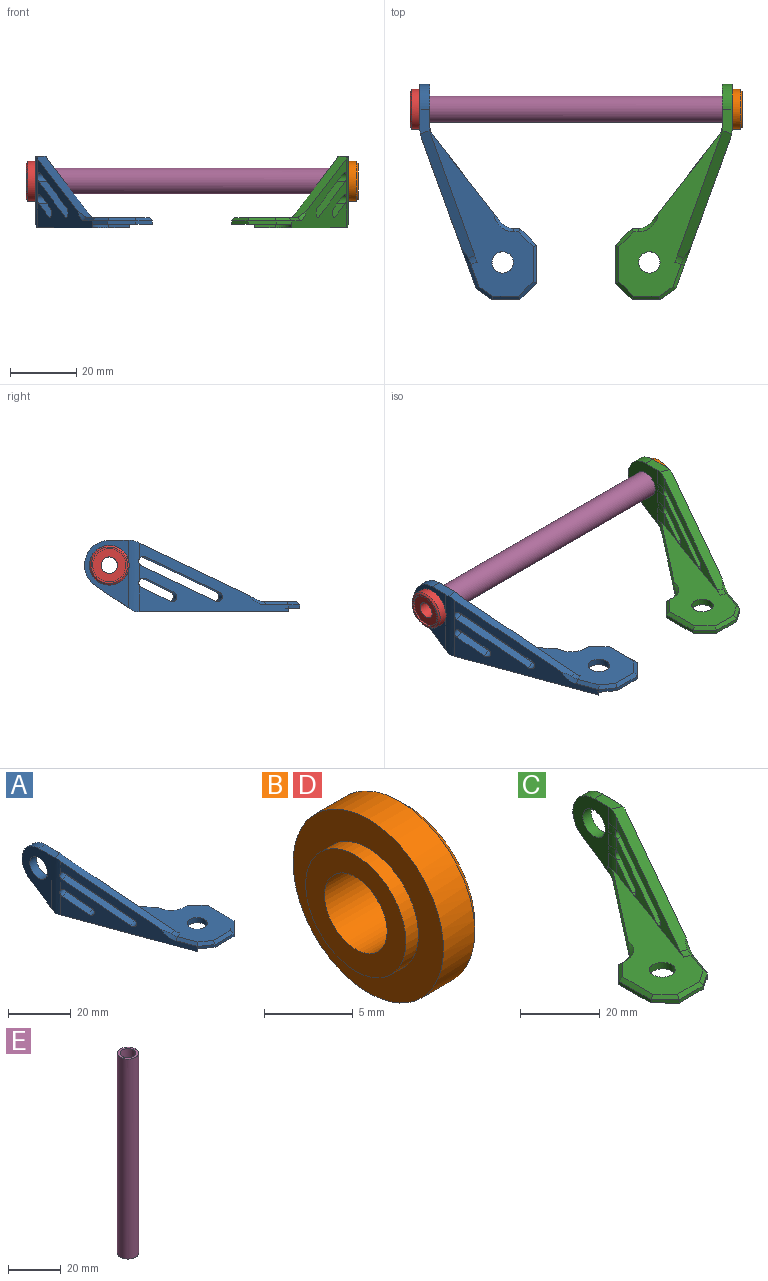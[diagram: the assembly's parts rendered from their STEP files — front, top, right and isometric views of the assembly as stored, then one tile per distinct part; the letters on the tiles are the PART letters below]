
ASSEMBLY  parts=5 mates=3
PART A: 51 faces, bbox 35.9x65.7x22.2 mm
  f0: plane 11.45x1mm, normal (1,0,0), area 11.4mm2, adj f35,f36,f40,f46
  f1: cylinder r=3.23mm len=6.45mm, axis (0,0,-1), area 40.5mm2, adj f2,f40
  f2: plane 51.56x31.22mm, normal (0,0,1), area 480.9mm2, adj f1,f6,f7,f8,f12,f24,f26,f33
  f3: plane 8.52x1mm, normal (0,-1,0), area 8.5mm2, adj f34,f36,f40,f44
  f4: plane 46.71x28.19mm, normal (0,0,-1), area 339.8mm2, adj f5,f9,f25,f32,f33,f37,f38,f39
  f5: plane 11.72x7.82mm, normal (0,0.55,-0.83), area 42.6mm2, adj f4,f8,f11,f13,f25,f50
  f6: plane 37.58x17.47mm, normal (0.94,0.34,0), area 123.7mm2, adj f2,f15,f17,f18,f19,f24,f30
  f7: plane 23.11x10.9mm, normal (0.94,0.34,0), area 75.5mm2, adj f2,f16,f17,f19,f21,f22,f23,f28
  f8: plane 19.79x12.83mm, normal (1,0,0), area 135.2mm2, adj f2,f5,f10,f13,f14,f26,f27,f28
  f9: plane 45.05x20.71mm, normal (-0.94,-0.34,0), area 358.8mm2, adj f4,f15,f16,f17,f18,f19,f20,f21
  f10: plane 7.45x3.07mm, normal (0,0,1), area 20.8mm2, adj f8,f11,f13,f15,f25,f30
  f11: plane 20.33x13.24mm, normal (-1,0,0), area 146mm2, adj f5,f10,f13,f14,f25
  f12: plane 9.34x4.32mm, normal (0.94,0.34,0), area 20.8mm2, adj f2,f20,f21,f23,f26
  f13: cylinder r=7.5mm len=13.74mm, axis (-1,0,0), area 57.5mm2, adj f5,f8,f10,f11
  f14: cylinder r=4mm len=8mm, axis (-1,0,0), area 75.4mm2, adj f8,f11
  f15: plane 39.31x18.79mm, normal (0.14,-0.38,0.91), area 130.3mm2, adj f6,f9,f10,f24,f25,f30,f41
  f16: plane 23.47x10.99mm, normal (0.14,-0.38,0.91), area 78.5mm2, adj f7,f9,f17,f19
  f17: cylinder r=1.5mm len=3.54mm, axis (-0.94,-0.34,0), area 14.1mm2, adj f6,f7,f9,f16,f18,f25,f29
  f18: plane 23.47x10.99mm, normal (-0.14,0.38,-0.91), area 78.5mm2, adj f6,f9,f17,f19
  f19: cylinder r=1.5mm len=3.54mm, axis (-0.94,-0.34,0), area 14.1mm2, adj f6,f7,f9,f16,f18
  f20: plane 9.7x5.98mm, normal (0.14,-0.38,0.91), area 30.4mm2, adj f9,f12,f21,f23
  f21: cylinder r=1.5mm len=3.54mm, axis (-0.94,-0.34,0), area 14.1mm2, adj f7,f9,f12,f20,f22,f25,f27
  f22: plane 9.7x5.98mm, normal (-0.14,0.38,-0.91), area 30.4mm2, adj f7,f9,f21,f23
  f23: cylinder r=1.5mm len=3.54mm, axis (-0.94,-0.34,0), area 14.1mm2, adj f7,f9,f12,f20,f22
  f24: cylinder r=5mm len=2.61mm, axis (0.94,0.34,0), area 4.2mm2, adj f2,f6,f15,f41
  f25: cylinder r=10mm len=21.5mm, axis (0,0,1), area 72.7mm2, adj f4,f5,f9,f10,f11,f15,f17,f21
  f26: cylinder r=10mm len=4.32mm, axis (0,0,-1), area 15.1mm2, adj f2,f8,f12,f27
  f27: bspline ~3.53x3.06mm, area 7.6mm2, adj f8,f21,f26,f28
  f28: cylinder r=10mm len=3.93mm, axis (0,0,-1), area 13.7mm2, adj f7,f8,f27,f29
  f29: bspline ~3.59x3.42mm, area 7.6mm2, adj f8,f17,f28,f30
  f30: cylinder r=10mm len=4.96mm, axis (0,0,-1), area 16.1mm2, adj f6,f8,f10,f15,f29
  f31: plane 1.87x1mm, normal (0,1,0), area 1.9mm2, adj f32,f35,f40,f48
  f32: cylinder r=5mm len=3.94mm, axis (0,0,1), area 9.1mm2, adj f4,f31,f33,f37,f49
  f33: plane 26.84x21.07mm, normal (0.79,0.61,0), area 97.1mm2, adj f2,f4,f32,f49,f50
  f34: plane 4.7x3.29mm, normal (-0.57,-0.82,0), area 5.7mm2, adj f3,f9,f40,f43
  f35: plane 5x5mm, normal (0.71,0.71,0), area 7.1mm2, adj f0,f31,f40,f47
  f36: plane 5x5mm, normal (0.71,-0.71,0), area 7.1mm2, adj f0,f3,f40,f45
  f37: plane 6.34x1mm, normal (0,-1,0), area 6.3mm2, adj f4,f32,f38,f40
  f38: cylinder r=5mm len=5mm, axis (0,0,-1), area 7.9mm2, adj f4,f37,f39,f40
  f39: plane 13.16x1mm, normal (1,0,0), area 13.2mm2, adj f4,f9,f38,f40
  f40: plane 21.45x18.22mm, normal (0,0,-1), area 320mm2, adj f0,f1,f3,f31,f34,f35,f36,f37
  f41: cone r=6mm half-angle=45deg, axis (-0.94,-0.34,0), area 5.6mm2, adj f9,f15,f24,f42
  f42: plane 7.32x3.37mm, normal (-0.66,-0.24,0.71), area 10.3mm2, adj f2,f9,f41,f43
  f43: plane 5.01x3.93mm, normal (-0.41,-0.58,0.71), area 7.7mm2, adj f2,f34,f42,f44
  f44: plane 8.52x1mm, normal (0,-0.71,0.71), area 11.5mm2, adj f2,f3,f43,f45
  f45: plane 5.41x5.41mm, normal (0.5,-0.5,0.71), area 9.4mm2, adj f2,f36,f44,f46
  f46: plane 11.45x1mm, normal (0.71,0,0.71), area 15.6mm2, adj f0,f2,f45,f47
  f47: plane 5.41x5.41mm, normal (0.5,0.5,0.71), area 9.4mm2, adj f2,f35,f46,f48
  f48: plane 1.87x1mm, normal (0,0.71,0.71), area 2.4mm2, adj f2,f31,f47,f49
  f49: cone r=5mm half-angle=45deg, axis (0,0,1), area 9.4mm2, adj f2,f32,f33,f48
  f50: cylinder r=5mm len=3.07mm, axis (0,0,-1), area 7.6mm2, adj f2,f4,f5,f8,f33
PART B: 9 faces, bbox 4x12x12 mm
  f0: cylinder r=4mm len=8mm, axis (-1,0,0), area 25.1mm2, adj f1,f7
  f1: plane 8x8mm, normal (-1,0,0), area 30.6mm2, adj f0,f2
  f2: cylinder r=2.5mm len=5mm, axis (-1,0,0), area 55mm2, adj f1,f3
  f3: plane 10x10mm, normal (1,0,0), area 58.9mm2, adj f2,f4
  f4: cylinder r=5mm len=10mm, axis (-1,0,0), area 15.7mm2, adj f3,f5
  f5: plane 11x11mm, normal (1,0,0), area 16.5mm2, adj f4,f8
  f6: cylinder r=6mm len=12mm, axis (-1,0,0), area 94.2mm2, adj f7,f8
  f7: plane 12x12mm, normal (-1,0,0), area 62.8mm2, adj f0,f6
  f8: cone r=6mm half-angle=45deg, axis (-1,0,0), area 25.5mm2, adj f5,f6
PART C: 51 faces, bbox 35.3x65.1x21.6 mm
  f0: plane 11.45x1mm, normal (-1,0,0), area 11.4mm2, adj f35,f36,f40,f46
  f1: cylinder r=3.23mm len=6.45mm, axis (0,0,-1), area 40.5mm2, adj f2,f40
  f2: plane 51.56x31.22mm, normal (0,0,1), area 480.9mm2, adj f1,f6,f7,f8,f12,f24,f26,f33
  f3: plane 8.52x1mm, normal (0,-1,0), area 8.5mm2, adj f34,f36,f40,f44
  f4: plane 46.71x28.19mm, normal (0,0,-1), area 339.8mm2, adj f5,f9,f25,f32,f33,f37,f38,f39
  f5: plane 11.72x7.82mm, normal (0,0.55,-0.83), area 42.6mm2, adj f4,f8,f11,f13,f25,f50
  f6: plane 37.58x17.47mm, normal (-0.94,0.34,0), area 123.7mm2, adj f2,f15,f17,f18,f19,f24,f30
  f7: plane 23.11x10.9mm, normal (-0.94,0.34,0), area 75.5mm2, adj f2,f16,f17,f19,f21,f22,f23,f28
  f8: plane 19.79x12.83mm, normal (-1,0,0), area 135.2mm2, adj f2,f5,f10,f13,f14,f26,f27,f28
  f9: plane 45.05x20.71mm, normal (0.94,-0.34,0), area 358.8mm2, adj f4,f15,f16,f17,f18,f19,f20,f21
  f10: plane 7.45x3.07mm, normal (0,0,1), area 20.8mm2, adj f8,f11,f13,f15,f25,f30
  f11: plane 20.33x13.24mm, normal (1,0,0), area 146mm2, adj f5,f10,f13,f14,f25
  f12: plane 9.34x4.32mm, normal (-0.94,0.34,0), area 20.8mm2, adj f2,f20,f21,f23,f26
  f13: cylinder r=7.5mm len=13.74mm, axis (1,0,0), area 57.5mm2, adj f5,f8,f10,f11
  f14: cylinder r=4mm len=8mm, axis (1,0,0), area 75.4mm2, adj f8,f11
  f15: plane 38.59x18.07mm, normal (-0.14,-0.38,0.91), area 130.3mm2, adj f6,f9,f10,f24,f25,f30,f41
  f16: plane 23.47x10.99mm, normal (-0.14,-0.38,0.91), area 78.5mm2, adj f7,f9,f17,f19
  f17: cylinder r=1.5mm len=3.54mm, axis (0.94,-0.34,0), area 14.1mm2, adj f6,f7,f9,f16,f18,f25,f29
  f18: plane 23.47x10.99mm, normal (0.14,0.38,-0.91), area 78.5mm2, adj f6,f9,f17,f19
  f19: cylinder r=1.5mm len=3.54mm, axis (0.94,-0.34,0), area 14.1mm2, adj f6,f7,f9,f16,f18
  f20: plane 9.7x5.98mm, normal (-0.14,-0.38,0.91), area 30.4mm2, adj f9,f12,f21,f23
  f21: cylinder r=1.5mm len=3.54mm, axis (0.94,-0.34,0), area 14.1mm2, adj f7,f9,f12,f20,f22,f25,f27
  f22: plane 9.7x5.98mm, normal (0.14,0.38,-0.91), area 30.4mm2, adj f7,f9,f21,f23
  f23: cylinder r=1.5mm len=3.54mm, axis (0.94,-0.34,0), area 14.1mm2, adj f7,f9,f12,f20,f22
  f24: cylinder r=5mm len=2.61mm, axis (-0.94,0.34,0), area 4.2mm2, adj f2,f6,f15,f41
  f25: cylinder r=10mm len=21.5mm, axis (0,0,1), area 72.7mm2, adj f4,f5,f9,f10,f11,f15,f17,f21
  f26: cylinder r=10mm len=4.32mm, axis (0,0,-1), area 15.1mm2, adj f2,f8,f12,f27
  f27: bspline ~3.53x3.06mm, area 7.6mm2, adj f8,f21,f26,f28
  f28: cylinder r=10mm len=3.93mm, axis (0,0,-1), area 13.7mm2, adj f7,f8,f27,f29
  f29: bspline ~3.59x3.42mm, area 7.6mm2, adj f8,f17,f28,f30
  f30: cylinder r=10mm len=4.96mm, axis (0,0,-1), area 16.1mm2, adj f6,f8,f10,f15,f29
  f31: plane 1.87x1mm, normal (0,1,0), area 1.9mm2, adj f32,f35,f40,f48
  f32: cylinder r=5mm len=3.94mm, axis (0,0,1), area 9.1mm2, adj f4,f31,f33,f37,f49
  f33: plane 26.11x20.34mm, normal (-0.79,0.61,0), area 97.1mm2, adj f2,f4,f32,f49,f50
  f34: plane 4.7x3.29mm, normal (0.57,-0.82,0), area 5.7mm2, adj f3,f9,f40,f43
  f35: plane 5x5mm, normal (-0.71,0.71,0), area 7.1mm2, adj f0,f31,f40,f47
  f36: plane 5x5mm, normal (-0.71,-0.71,0), area 7.1mm2, adj f0,f3,f40,f45
  f37: plane 6.34x1mm, normal (0,-1,0), area 6.3mm2, adj f4,f32,f38,f40
  f38: cylinder r=5mm len=5mm, axis (0,0,-1), area 7.9mm2, adj f4,f37,f39,f40
  f39: plane 13.16x1mm, normal (-1,0,0), area 13.2mm2, adj f4,f9,f38,f40
  f40: plane 21.45x18.22mm, normal (0,0,-1), area 320mm2, adj f0,f1,f3,f31,f34,f35,f36,f37
  f41: cone r=6mm half-angle=45deg, axis (0.94,-0.34,0), area 6.5mm2, adj f9,f15,f24,f42
  f42: plane 7.32x3.37mm, normal (0.66,-0.24,0.71), area 10.3mm2, adj f2,f9,f41,f43
  f43: plane 5.01x3.93mm, normal (0.41,-0.58,0.71), area 7.7mm2, adj f2,f34,f42,f44
  f44: plane 8.52x1mm, normal (0,-0.71,0.71), area 11.5mm2, adj f2,f3,f43,f45
  f45: plane 5.41x5.41mm, normal (-0.5,-0.5,0.71), area 9.4mm2, adj f2,f36,f44,f46
  f46: plane 11.45x1mm, normal (-0.71,0,0.71), area 15.6mm2, adj f0,f2,f45,f47
  f47: plane 5.41x5.41mm, normal (-0.5,0.5,0.71), area 9.4mm2, adj f2,f35,f46,f48
  f48: plane 1.87x1mm, normal (0,0.71,0.71), area 2.4mm2, adj f2,f31,f47,f49
  f49: cone r=5mm half-angle=45deg, axis (0,0,1), area 10.3mm2, adj f2,f32,f33,f48
  f50: cylinder r=5mm len=3.07mm, axis (0,0,-1), area 7.6mm2, adj f2,f4,f5,f8,f33
PART D: same geometry as B
PART E: 4 faces, bbox 8x8x92.3 mm
  f0: plane 8x8mm, normal (0,0,1), area 22mm2, adj f2,f3
  f1: plane 8x8mm, normal (0,0,-1), area 22mm2, adj f2,f3
  f2: cylinder r=4mm len=92.34mm, axis (0,0,-1), area 2320.7mm2, adj f0,f1
  f3: cylinder r=3mm len=92.34mm, axis (0,0,-1), area 1740.5mm2, adj f0,f1
PLACE A t=(-12.56,-15.6,8.64)mm
PLACE B t=(33.61,30.67,22.64)mm
PLACE C t=(-12.56,-15.6,8.64)mm
PLACE D rot(axis=(0,1,0),180deg) t=(-58.73,30.67,22.64)mm
PLACE E rot(axis=(0.71,0,-0.71),180deg) t=(33.61,30.67,22.64)mm
MATE fastened E.f3 <-> D.f0  axis (-1,0,0) through (-58.73,30.67,22.64)mm
MATE fastened D.f0 <-> A.f13  axis (1,0,0) through (-58.73,30.67,22.64)mm
MATE fastened B.f0 <-> C.f13  axis (-1,0,0) through (33.61,30.67,22.64)mm
